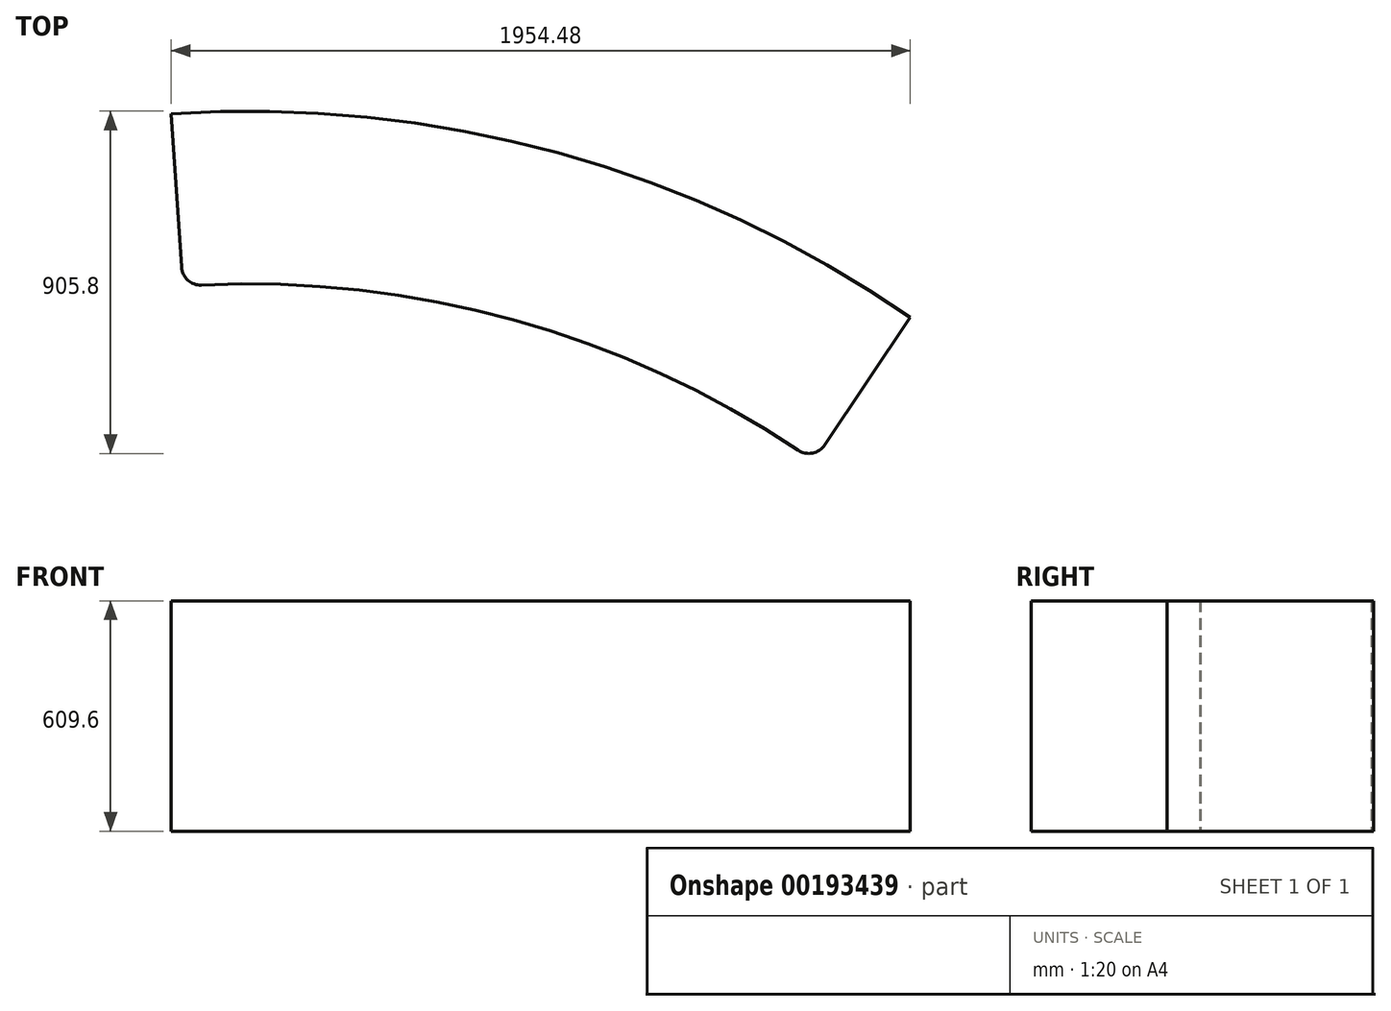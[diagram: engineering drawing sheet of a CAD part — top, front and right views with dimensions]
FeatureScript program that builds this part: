
annotation { "Feature Type Name" : "Feature", "Feature Type Description" : "" }
export const myFeature = defineFeature(function(context is Context, id is Id, definition is map)
    precondition{}
    {
        {
            var Q0;
            Q0=qCreatedBy(makeId("Top.planeOp"),FACE);
            var sketch = newSketch(context, id + "F0", { "sketchPlane" : qUnion([Q0])});
            skLineSegment(sketch, "E0", {"start": v(-2322.3, 99.74) * mm, "end": v(363.78, 99.74) * mm});
            skLineSegment(sketch, "E1", {"start": v(2078.28, -1614.76) * mm, "end": v(2078.28, -2224.36) * mm});
            skArc(sketch, "E2", {"start": v(2078.28, -1614.76) * mm, "mid": v(865.95, -1112.6) * mm, "end": v(363.78, 99.74) * mm});
            skArc(sketch, "E3.0", {"start": v(2078.28, -1919.56) * mm, "mid": v(1203.8, -1720.4) * mm, "end": v(501.84, -1162.16) * mm});
            skArc(sketch, "E4.0", {"start": v(2078.28, -2224.36) * mm, "mid": v(1071.81, -1995.13) * mm, "end": v(263.88, -1352.64) * mm});
            skLineSegment(sketch, "E5", {"start": v(-2322.3, 99.74) * mm, "end": v(-2341.12, -206.78) * mm});
            skPoint(sketch, "E6", {"position": v(-2322.3, 99.74) * mm});
            skArc(sketch, "E7", {"start": v(501.84, -1162.16) * mm, "mid": v(-757.31, -188.98) * mm, "end": v(-2322.3, 99.74) * mm});
            skArc(sketch, "E8.0", {"start": v(263.88, -1352.64) * mm, "mid": v(-898, -460.02) * mm, "end": v(-2341.12, -206.78) * mm});
            skPoint(sketch, "E9.orphan", {"position": v(-2399.79, -1162.16) * mm});
            skLineSegment(sketch, "E10", {"start": v(2078.28, 99.74) * mm, "end": v(0, -1978.55) * mm});
            skLineSegment(sketch, "E11", {"start": v(-2341.12, -206.78) * mm, "end": v(-2322.3, 99.74) * mm});
            skLineSegment(sketch, "E12", {"start": v(2078.28, -1614.76) * mm, "end": v(2052.9, -1614.09) * mm});
            skLineSegment(sketch, "E13.0", {"start": v(2052.88, -1614.09) * mm, "end": v(2052.88, -2223.26) * mm});
            skLineSegment(sketch, "E14", {"start": v(-2339.55, -181.22) * mm, "end": v(-2322.3, 99.74) * mm});
            skLineSegment(sketch, "E15", {"start": v(-2341.12, -206.78) * mm, "end": v(-2314.2, 100.17) * mm});
            skArc(sketch, "E16.0", {"start": v(-683.26, -1097.14) * mm, "mid": v(-1436.95, -752.06) * mm, "end": v(-2260.77, -660.1) * mm});
            skLineSegment(sketch, "E17", {"start": v(-612.87, -1083.19) * mm, "end": v(-386.64, -745.96) * mm, "construction": true});
            skLineSegment(sketch, "E18", {"start": v(-2341.12, -206.78) * mm, "end": v(-2313.9, -612.75) * mm});
            skLineSegment(sketch, "E19", {"start": v(-386.64, -745.96) * mm, "end": v(-616.4, -1088.46) * mm});
            skPoint(sketch, "E20.visualSharp", {"position": v(-2310.52, -662.96) * mm});
            skArc(sketch, "E20.filletArc", {"start": v(-2313.9, -612.75) * mm, "mid": v(-2297, -647.28) * mm, "end": v(-2260.77, -660.1) * mm});
            skArc(sketch, "E21.filletArc", {"start": v(-683.26, -1097.14) * mm, "mid": v(-645.18, -1104.72) * mm, "end": v(-612.87, -1083.19) * mm});
            skSolve(sketch);
        }
        {
            var Q0;
            Q0=makeQuery(id+"F0.imprint","IMPRINT",FACE,{"disambiguationData":[TD([[makeQuery(id+"F0.imprint","IMPRINT",EDGE,{"derivedFrom":sQuery(id+"F0.wireOp",EDGE,"E16.0")}),-1.0]])]});
            extrude(context, id + "F1", {"entities" : qUnion([Q0]), "depth" : 609.6 * mm});
        }
    });
